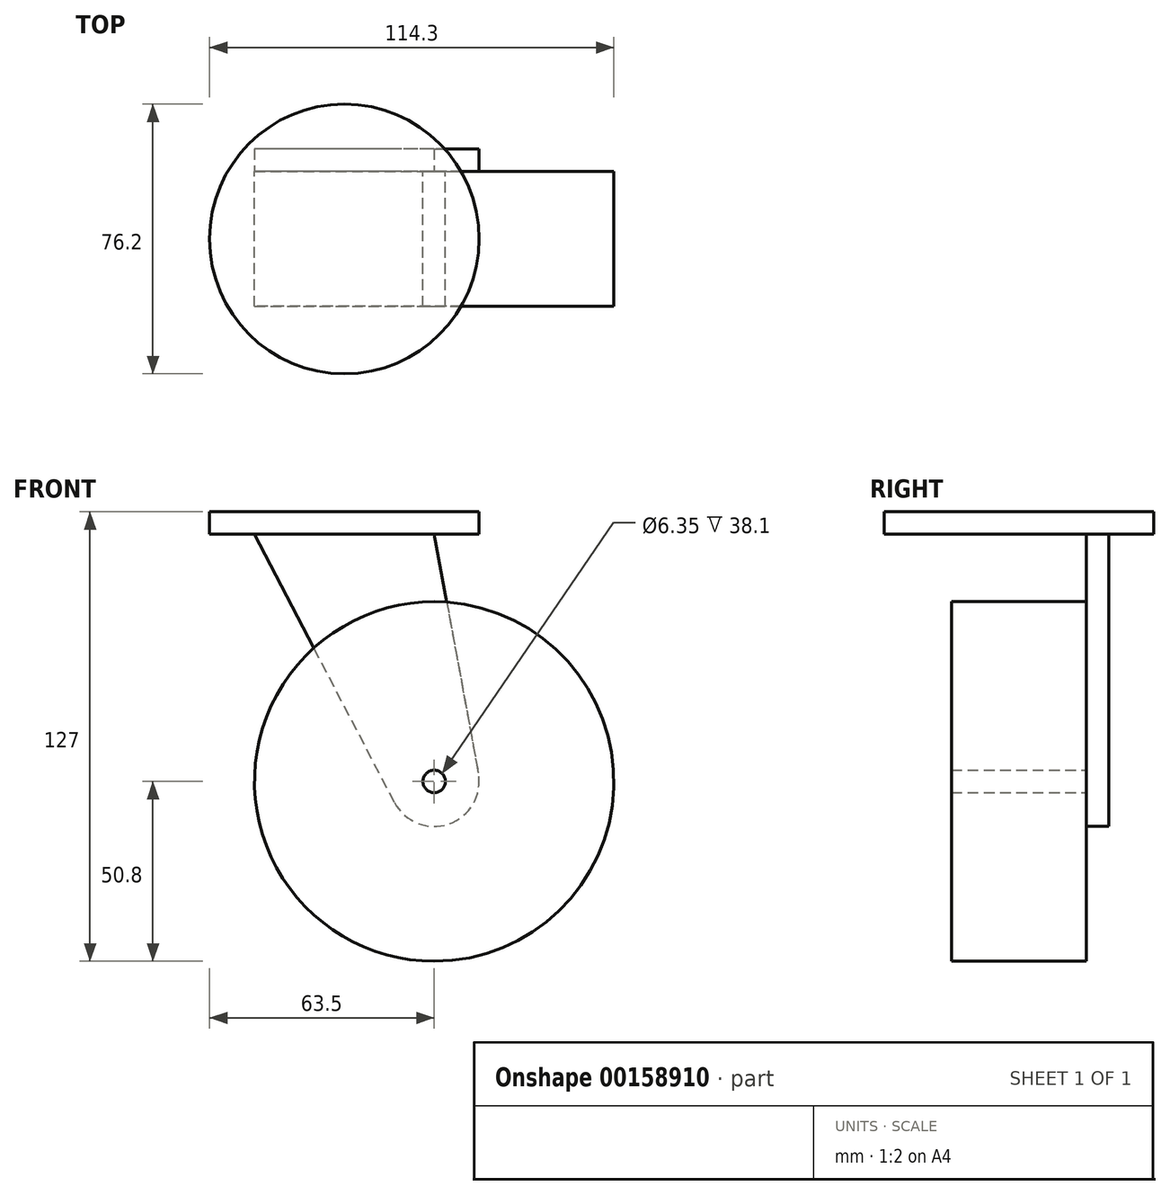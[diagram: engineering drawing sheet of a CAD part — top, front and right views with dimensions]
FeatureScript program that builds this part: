
annotation { "Feature Type Name" : "Feature", "Feature Type Description" : "" }
export const myFeature = defineFeature(function(context is Context, id is Id, definition is map)
    precondition{}
    {
        {
            var Q0;
            Q0=qCreatedBy(makeId("Front.planeOp"),FACE);
            var sketch = newSketch(context, id + "F0", { "sketchPlane" : qUnion([Q0])});
            skCircle(sketch, "E0", {"center": v(0, 0) * mm, "radius": 3.18 * mm});
            skCircle(sketch, "E1", {"center": v(0, 0) * mm, "radius": 50.8 * mm});
            skSolve(sketch);
        }
        {
            var Q0;
            Q0=makeQuery(id+"F0.imprint","IMPRINT",FACE,{"disambiguationData":[TD([[makeQuery(id+"F0.imprint","IMPRINT",EDGE,{"derivedFrom":sQuery(id+"F0.wireOp",EDGE,"E0")}),-1.0]])]});
            extrude(context, id + "F1", {"entities" : qUnion([Q0]), "endBound" : BoundingType.SYMMETRIC, "depth" : 38.1 * mm});
        }
        {
            var Q0;
            Q0=qCreatedBy(makeId("Top.planeOp"),FACE);
            cPlane(context, id + "F2", {"entities" : qUnion([Q0]), "cplaneType" : CPlaneType.OFFSET, "offset" : 76.2 * mm, "width" : 152.4 * mm, "height" : 152.4 * mm});
        }
        {
            var Q0;
            Q0=qCreatedBy(id+"F2.planeOp",FACE);
            var sketch = newSketch(context, id + "F3", { "sketchPlane" : qUnion([Q0])});
            skCircle(sketch, "E2", {"center": v(-25.4, 0) * mm, "radius": 38.1 * mm});
            skSolve(sketch);
        }
        {
            var Q0;
            Q0=makeQuery(id+"F3.imprint","IMPRINT",FACE,{"disambiguationData":[TD([[makeQuery(id+"F3.imprint","IMPRINT",EDGE,{"derivedFrom":sQuery(id+"F3.wireOp",EDGE,"E2")}),1.0]])]});
            extrude(context, id + "F4", {"entities" : qUnion([Q0]), "oppositeDirection" : true, "depth" : 6.35 * mm});
        }
        {
            var Q0;
            Q0=makeQuery(id+"F1.opExtrude","CAP_FACE",FACE,{"disambiguationData":[OSD([sQuery(id+"F0.wireOp",EDGE,"E0"),sQuery(id+"F0.wireOp",EDGE,"E1")])],"isStart":true});
            var sketch = newSketch(context, id + "F5", { "sketchPlane" : qUnion([Q0])});
            skArc(sketch, "E3", {"start": v(-12.49, 2.3) * mm, "mid": v(-4.14, -12) * mm, "end": v(11.26, -5.88) * mm});
            skLineSegment(sketch, "E4", {"start": v(0, 69.85) * mm, "end": v(-12.49, 2.3) * mm});
            skLineSegment(sketch, "E5", {"start": v(11.26, -5.88) * mm, "end": v(50.8, 69.85) * mm});
            skLineSegment(sketch, "E6", {"start": v(0, 69.85) * mm, "end": v(50.8, 69.85) * mm});
            skPoint(sketch, "E7", {"position": v(25.4, 69.85) * mm});
            skSolve(sketch);
        }
        {
            var Q0;
            Q0 = qSketchRegion(id + "F5", true);
            extrude(context, id + "F6", {"entities" : qUnion([Q0]), "operationType" : NewBodyOperationType.ADD, "depth" : 6.35 * mm});
        }
    });
